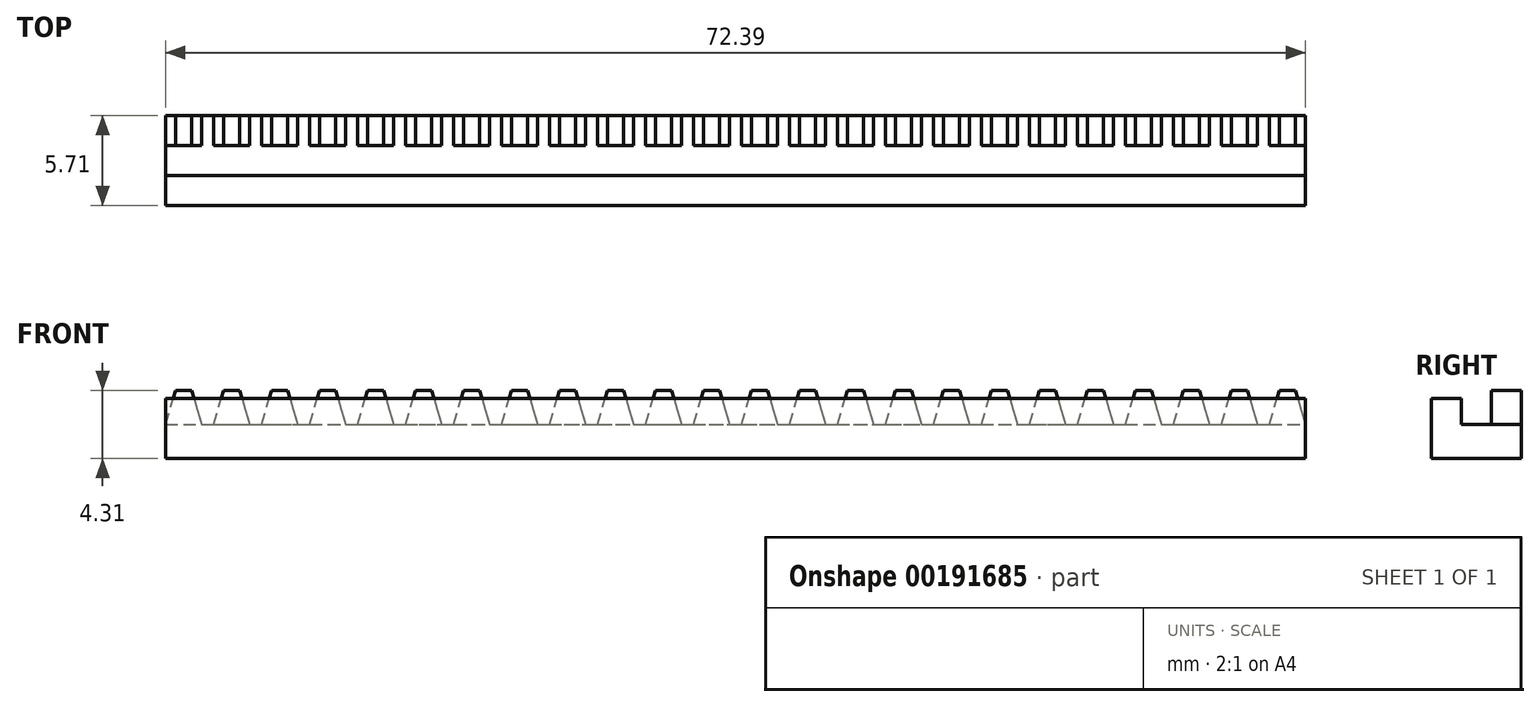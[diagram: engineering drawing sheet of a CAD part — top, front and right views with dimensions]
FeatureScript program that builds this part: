
annotation { "Feature Type Name" : "Feature", "Feature Type Description" : "" }
export const myFeature = defineFeature(function(context is Context, id is Id, definition is map)
    precondition{}
    {
        {
            var Q0;
            Q0=qCreatedBy(makeId("Front.planeOp"),FACE);
            var sketch = newSketch(context, id + "F0", { "sketchPlane" : qUnion([Q0])});
            skLineSegment(sketch, "E0.top", {"start": v(-38.44, 16.9) * mm, "end": v(33.18, 16.9) * mm});
            skLineSegment(sketch, "E0.left", {"start": v(-38.44, 12.58) * mm, "end": v(-38.44, 16.9) * mm});
            skLineSegment(sketch, "E1", {"start": v(-38.44, 16.9) * mm, "end": v(-37.17, 21.21) * mm});
            skLineSegment(sketch, "E2", {"start": v(-37.17, 21.21) * mm, "end": v(-35.14, 21.21) * mm});
            skLineSegment(sketch, "E3", {"start": v(-35.14, 21.21) * mm, "end": v(-33.87, 16.9) * mm});
            skLineSegment(sketch, "E4", {"start": v(-38.44, 16.9) * mm, "end": v(-33.87, 16.9) * mm});
            skLineSegment(sketch, "E5", {"start": v(-36.16, 21.21) * mm, "end": v(-36.16, 16.9) * mm, "construction": true});
            skLineSegment(sketch, "E6.1.0.0", {"start": v(-29.05, 21.21) * mm, "end": v(-27.78, 16.9) * mm});
            skLineSegment(sketch, "E6.1.0.1", {"start": v(-32.35, 16.9) * mm, "end": v(-31.08, 21.21) * mm});
            skLineSegment(sketch, "E6.1.0.2", {"start": v(-31.08, 21.21) * mm, "end": v(-29.05, 21.21) * mm});
            skLineSegment(sketch, "E6.2.0.0", {"start": v(-22.95, 21.21) * mm, "end": v(-21.68, 16.9) * mm});
            skLineSegment(sketch, "E6.2.0.1", {"start": v(-26.25, 16.9) * mm, "end": v(-24.98, 21.21) * mm});
            skLineSegment(sketch, "E6.2.0.2", {"start": v(-24.98, 21.21) * mm, "end": v(-22.95, 21.21) * mm});
            skLineSegment(sketch, "E6.3.0.0", {"start": v(-16.85, 21.21) * mm, "end": v(-15.58, 16.9) * mm});
            skLineSegment(sketch, "E6.3.0.1", {"start": v(-20.16, 16.9) * mm, "end": v(-18.89, 21.21) * mm});
            skLineSegment(sketch, "E6.3.0.2", {"start": v(-18.89, 21.21) * mm, "end": v(-16.85, 21.21) * mm});
            skLineSegment(sketch, "E6.4.0.0", {"start": v(-10.76, 21.21) * mm, "end": v(-9.49, 16.9) * mm});
            skLineSegment(sketch, "E6.4.0.1", {"start": v(-14.06, 16.9) * mm, "end": v(-12.8, 21.21) * mm});
            skLineSegment(sketch, "E6.4.0.2", {"start": v(-12.8, 21.21) * mm, "end": v(-10.76, 21.21) * mm});
            skLineSegment(sketch, "E6.5.0.0", {"start": v(-4.66, 21.21) * mm, "end": v(-3.4, 16.9) * mm});
            skLineSegment(sketch, "E6.5.0.1", {"start": v(-7.96, 16.9) * mm, "end": v(-6.7, 21.21) * mm});
            skLineSegment(sketch, "E6.5.0.2", {"start": v(-6.7, 21.21) * mm, "end": v(-4.66, 21.21) * mm});
            skLineSegment(sketch, "E6.6.0.0", {"start": v(1.43, 21.21) * mm, "end": v(2.7, 16.9) * mm});
            skLineSegment(sketch, "E6.6.0.1", {"start": v(-1.87, 16.9) * mm, "end": v(-0.6, 21.21) * mm});
            skLineSegment(sketch, "E6.6.0.2", {"start": v(-0.6, 21.21) * mm, "end": v(1.43, 21.21) * mm});
            skLineSegment(sketch, "E6.7.0.0", {"start": v(7.53, 21.21) * mm, "end": v(8.8, 16.9) * mm});
            skLineSegment(sketch, "E6.7.0.1", {"start": v(4.23, 16.9) * mm, "end": v(5.5, 21.21) * mm});
            skLineSegment(sketch, "E6.7.0.2", {"start": v(5.5, 21.21) * mm, "end": v(7.53, 21.21) * mm});
            skLineSegment(sketch, "E6.8.0.0", {"start": v(13.63, 21.21) * mm, "end": v(14.9, 16.9) * mm});
            skLineSegment(sketch, "E6.8.0.1", {"start": v(10.32, 16.9) * mm, "end": v(11.6, 21.21) * mm});
            skLineSegment(sketch, "E6.8.0.2", {"start": v(11.6, 21.21) * mm, "end": v(13.63, 21.21) * mm});
            skLineSegment(sketch, "E6.9.0.0", {"start": v(19.72, 21.21) * mm, "end": v(21, 16.9) * mm});
            skLineSegment(sketch, "E6.9.0.1", {"start": v(16.42, 16.9) * mm, "end": v(17.69, 21.21) * mm});
            skLineSegment(sketch, "E6.9.0.2", {"start": v(17.69, 21.21) * mm, "end": v(19.72, 21.21) * mm});
            skLineSegment(sketch, "E6.10.0.0", {"start": v(25.82, 21.21) * mm, "end": v(27.09, 16.9) * mm});
            skLineSegment(sketch, "E6.10.0.1", {"start": v(22.52, 16.9) * mm, "end": v(23.79, 21.21) * mm});
            skLineSegment(sketch, "E6.10.0.2", {"start": v(23.79, 21.21) * mm, "end": v(25.82, 21.21) * mm});
            skLineSegment(sketch, "E6.11.0.0", {"start": v(31.91, 21.21) * mm, "end": v(33.18, 16.9) * mm});
            skLineSegment(sketch, "E6.11.0.1", {"start": v(28.61, 16.9) * mm, "end": v(29.88, 21.21) * mm});
            skLineSegment(sketch, "E6.11.0.2", {"start": v(29.88, 21.21) * mm, "end": v(31.91, 21.21) * mm});
            skLineSegment(sketch, "E6.direction1", {"start": v(-38.44, 16.9) * mm, "end": v(-32.35, 16.9) * mm, "construction": true});
            skPoint(sketch, "E7.centerSnap0", {"position": v(-38.44, 14.74) * mm});
            skLineSegment(sketch, "E8.0.12.0", {"start": v(38, 21.21) * mm, "end": v(39.28, 16.9) * mm});
            skLineSegment(sketch, "E8.3.12.0", {"start": v(34.7, 16.9) * mm, "end": v(35.98, 21.21) * mm});
            skLineSegment(sketch, "E8.6.12.0", {"start": v(35.98, 21.21) * mm, "end": v(38, 21.21) * mm});
            skLineSegment(sketch, "E8.0.13.0", {"start": v(44.1, 21.21) * mm, "end": v(45.38, 16.9) * mm});
            skLineSegment(sketch, "E8.3.13.0", {"start": v(40.8, 16.9) * mm, "end": v(42.07, 21.21) * mm});
            skLineSegment(sketch, "E8.6.13.0", {"start": v(42.07, 21.21) * mm, "end": v(44.1, 21.21) * mm});
            skLineSegment(sketch, "E8.0.14.0", {"start": v(50.2, 21.21) * mm, "end": v(51.47, 16.9) * mm});
            skLineSegment(sketch, "E8.3.14.0", {"start": v(46.9, 16.9) * mm, "end": v(48.17, 21.21) * mm});
            skLineSegment(sketch, "E8.6.14.0", {"start": v(48.17, 21.21) * mm, "end": v(50.2, 21.21) * mm});
            skLineSegment(sketch, "E8.0.15.0", {"start": v(56.3, 21.21) * mm, "end": v(57.57, 16.9) * mm});
            skLineSegment(sketch, "E8.3.15.0", {"start": v(53, 16.9) * mm, "end": v(54.27, 21.21) * mm});
            skLineSegment(sketch, "E8.6.15.0", {"start": v(54.27, 21.21) * mm, "end": v(56.3, 21.21) * mm});
            skLineSegment(sketch, "E8.0.16.0", {"start": v(62.4, 21.21) * mm, "end": v(63.66, 16.9) * mm});
            skLineSegment(sketch, "E8.3.16.0", {"start": v(59.1, 16.9) * mm, "end": v(60.36, 21.21) * mm});
            skLineSegment(sketch, "E8.6.16.0", {"start": v(60.36, 21.21) * mm, "end": v(62.4, 21.21) * mm});
            skLineSegment(sketch, "E8.0.17.0", {"start": v(68.49, 21.21) * mm, "end": v(69.76, 16.9) * mm});
            skLineSegment(sketch, "E8.3.17.0", {"start": v(65.19, 16.9) * mm, "end": v(66.46, 21.21) * mm});
            skLineSegment(sketch, "E8.6.17.0", {"start": v(66.46, 21.21) * mm, "end": v(68.49, 21.21) * mm});
            skLineSegment(sketch, "E8.0.18.0", {"start": v(74.59, 21.21) * mm, "end": v(75.86, 16.9) * mm});
            skLineSegment(sketch, "E8.3.18.0", {"start": v(71.28, 16.9) * mm, "end": v(72.55, 21.21) * mm});
            skLineSegment(sketch, "E8.6.18.0", {"start": v(72.55, 21.21) * mm, "end": v(74.59, 21.21) * mm});
            skLineSegment(sketch, "E8.0.19.0", {"start": v(80.68, 21.21) * mm, "end": v(81.95, 16.9) * mm});
            skLineSegment(sketch, "E8.3.19.0", {"start": v(77.38, 16.9) * mm, "end": v(78.65, 21.21) * mm});
            skLineSegment(sketch, "E8.6.19.0", {"start": v(78.65, 21.21) * mm, "end": v(80.68, 21.21) * mm});
            skLineSegment(sketch, "E8.0.20.0", {"start": v(86.78, 21.21) * mm, "end": v(88.05, 16.9) * mm});
            skLineSegment(sketch, "E8.3.20.0", {"start": v(83.48, 16.9) * mm, "end": v(84.75, 21.21) * mm});
            skLineSegment(sketch, "E8.6.20.0", {"start": v(84.75, 21.21) * mm, "end": v(86.78, 21.21) * mm});
            skLineSegment(sketch, "E8.0.21.0", {"start": v(92.87, 21.21) * mm, "end": v(94.14, 16.9) * mm});
            skLineSegment(sketch, "E8.3.21.0", {"start": v(89.57, 16.9) * mm, "end": v(90.84, 21.21) * mm});
            skLineSegment(sketch, "E8.6.21.0", {"start": v(90.84, 21.21) * mm, "end": v(92.87, 21.21) * mm});
            skLineSegment(sketch, "E8.0.22.0", {"start": v(98.97, 21.21) * mm, "end": v(100.24, 16.9) * mm});
            skLineSegment(sketch, "E8.3.22.0", {"start": v(95.67, 16.9) * mm, "end": v(96.94, 21.21) * mm});
            skLineSegment(sketch, "E8.6.22.0", {"start": v(96.94, 21.21) * mm, "end": v(98.97, 21.21) * mm});
            skLineSegment(sketch, "E8.0.23.0", {"start": v(105.07, 21.21) * mm, "end": v(106.34, 16.9) * mm});
            skLineSegment(sketch, "E8.3.23.0", {"start": v(101.76, 16.9) * mm, "end": v(103.03, 21.21) * mm});
            skLineSegment(sketch, "E8.6.23.0", {"start": v(103.03, 21.21) * mm, "end": v(105.07, 21.21) * mm});
            skLineSegment(sketch, "E9", {"start": v(33.18, 16.9) * mm, "end": v(106.34, 16.9) * mm});
            skLineSegment(sketch, "E10", {"start": v(-38.44, 12.58) * mm, "end": v(106.34, 12.58) * mm});
            skLineSegment(sketch, "E11", {"start": v(106.34, 12.58) * mm, "end": v(106.34, 16.9) * mm});
            skSolve(sketch);
        }
        {
            var Q0;
            Q0=qSketchRegion(id+"F0",true);
            extrude(context, id + "F1", {"entities" : qUnion([Q0]), "depth" : 3.8 * mm});
        }
        {
            var Q0;
            Q0=qCreatedBy(makeId("Right.planeOp"),FACE);
            var Q1;
            Q1=makeQuery(id+"F1.opExtrude","CAP_VERTEX",VERTEX,{"disambiguationData":[OSD([sQuery(id+"F0.wireOp",EDGE,"E10"),sQuery(id+"F0.wireOp",EDGE,"E11")])],"isStart":false});
            cPlane(context, id + "F2", {"entities" : qUnion([Q0, Q1]), "cplaneType" : CPlaneType.PLANE_POINT, "offset" : 25.4 * mm, "width" : 152.4 * mm, "height" : 152.4 * mm});
        }
        {
            var Q0;
            Q0=qCreatedBy(id+"F2.planeOp",FACE);
            var sketch = newSketch(context, id + "F3", { "sketchPlane" : qUnion([Q0])});
            skLineSegment(sketch, "E12", {"start": v(-15.24, 16.39) * mm, "end": v(-11.43, 16.39) * mm});
            skLineSegment(sketch, "E13", {"start": v(-7.62, 16.9) * mm, "end": v(-7.62, 20.2) * mm});
            skLineSegment(sketch, "E14", {"start": v(-7.62, 20.2) * mm, "end": v(-11.43, 20.2) * mm});
            skLineSegment(sketch, "E15", {"start": v(-11.43, 20.2) * mm, "end": v(-11.43, 16.39) * mm});
            skLineSegment(sketch, "E16", {"start": v(-3.81, 12.58) * mm, "end": v(-15.24, 12.58) * mm});
            skLineSegment(sketch, "E17", {"start": v(-15.24, 12.58) * mm, "end": v(-15.24, 16.39) * mm});
            skLineSegment(sketch, "E18.0", {"start": v(-3.81, 12.58) * mm, "end": v(-3.81, 16.9) * mm});
            skLineSegment(sketch, "E19", {"start": v(-3.81, 16.9) * mm, "end": v(-7.62, 16.9) * mm});
            skLineSegment(sketch, "E20", {"start": v(-11.43, 16.39) * mm, "end": v(-11.43, 12.58) * mm});
            skSolve(sketch);
        }
        {
            var Q0;
            Q0=makeQuery(id+"F3.imprint","IMPRINT",FACE,{"disambiguationData":[TD([[makeQuery(id+"F3.imprint","IMPRINT",EDGE,{"derivedFrom":sQuery(id+"F3.wireOp",EDGE,"E13")}),1.0]])]});
            var Q1;
            Q1=makeQuery(id+"F1.opExtrude","SWEPT_FACE",FACE,{"disambiguationData":[OSD([sQuery(id+"F0.wireOp",EDGE,"E0.left")])]});
            extrude(context, id + "F4", {"entities" : qUnion([Q0]), "operationType" : NewBodyOperationType.ADD, "endBound" : BoundingType.UP_TO_SURFACE, "oppositeDirection" : true, "endBoundEntityFace" : qUnion([Q1]), "depth" : 33.02 * mm});
        }
        {
            var Q0;
            Q0=makeQuery(id+"F1.opExtrude","SWEPT_BODY",BODY,{"disambiguationData":[OSD([sQuery(id+"F0.wireOp",EDGE,"E0.top"),sQuery(id+"F0.wireOp",EDGE,"E0.left"),sQuery(id+"F0.wireOp",EDGE,"E1"),sQuery(id+"F0.wireOp",EDGE,"E2"),sQuery(id+"F0.wireOp",EDGE,"E3"),sQuery(id+"F0.wireOp",EDGE,"E6.1.0.0"),sQuery(id+"F0.wireOp",EDGE,"E6.1.0.1"),sQuery(id+"F0.wireOp",EDGE,"E6.1.0.2"),sQuery(id+"F0.wireOp",EDGE,"E6.2.0.0"),sQuery(id+"F0.wireOp",EDGE,"E6.2.0.1"),sQuery(id+"F0.wireOp",EDGE,"E6.2.0.2"),sQuery(id+"F0.wireOp",EDGE,"E6.3.0.0"),sQuery(id+"F0.wireOp",EDGE,"E6.3.0.1"),sQuery(id+"F0.wireOp",EDGE,"E6.3.0.2"),sQuery(id+"F0.wireOp",EDGE,"E6.4.0.0"),sQuery(id+"F0.wireOp",EDGE,"E6.4.0.1"),sQuery(id+"F0.wireOp",EDGE,"E6.4.0.2"),sQuery(id+"F0.wireOp",EDGE,"E6.5.0.0"),sQuery(id+"F0.wireOp",EDGE,"E6.5.0.1"),sQuery(id+"F0.wireOp",EDGE,"E6.5.0.2"),sQuery(id+"F0.wireOp",EDGE,"E6.6.0.0"),sQuery(id+"F0.wireOp",EDGE,"E6.6.0.1"),sQuery(id+"F0.wireOp",EDGE,"E6.6.0.2"),sQuery(id+"F0.wireOp",EDGE,"E6.7.0.0"),sQuery(id+"F0.wireOp",EDGE,"E6.7.0.1"),sQuery(id+"F0.wireOp",EDGE,"E6.7.0.2"),sQuery(id+"F0.wireOp",EDGE,"E6.8.0.0"),sQuery(id+"F0.wireOp",EDGE,"E6.8.0.1"),sQuery(id+"F0.wireOp",EDGE,"E6.8.0.2"),sQuery(id+"F0.wireOp",EDGE,"E6.9.0.0"),sQuery(id+"F0.wireOp",EDGE,"E6.9.0.1"),sQuery(id+"F0.wireOp",EDGE,"E6.9.0.2"),sQuery(id+"F0.wireOp",EDGE,"E6.10.0.0"),sQuery(id+"F0.wireOp",EDGE,"E6.10.0.1"),sQuery(id+"F0.wireOp",EDGE,"E6.10.0.2"),sQuery(id+"F0.wireOp",EDGE,"E6.11.0.0"),sQuery(id+"F0.wireOp",EDGE,"E6.11.0.1"),sQuery(id+"F0.wireOp",EDGE,"E6.11.0.2"),sQuery(id+"F0.wireOp",EDGE,"E8.0.12.0"),sQuery(id+"F0.wireOp",EDGE,"E8.3.12.0"),sQuery(id+"F0.wireOp",EDGE,"E8.6.12.0"),sQuery(id+"F0.wireOp",EDGE,"E8.0.13.0"),sQuery(id+"F0.wireOp",EDGE,"E8.3.13.0"),sQuery(id+"F0.wireOp",EDGE,"E8.6.13.0"),sQuery(id+"F0.wireOp",EDGE,"E8.0.14.0"),sQuery(id+"F0.wireOp",EDGE,"E8.3.14.0"),sQuery(id+"F0.wireOp",EDGE,"E8.6.14.0"),sQuery(id+"F0.wireOp",EDGE,"E8.0.15.0"),sQuery(id+"F0.wireOp",EDGE,"E8.3.15.0"),sQuery(id+"F0.wireOp",EDGE,"E8.6.15.0"),sQuery(id+"F0.wireOp",EDGE,"E8.0.16.0"),sQuery(id+"F0.wireOp",EDGE,"E8.3.16.0"),sQuery(id+"F0.wireOp",EDGE,"E8.6.16.0"),sQuery(id+"F0.wireOp",EDGE,"E8.0.17.0"),sQuery(id+"F0.wireOp",EDGE,"E8.3.17.0"),sQuery(id+"F0.wireOp",EDGE,"E8.6.17.0"),sQuery(id+"F0.wireOp",EDGE,"E8.0.18.0"),sQuery(id+"F0.wireOp",EDGE,"E8.3.18.0"),sQuery(id+"F0.wireOp",EDGE,"E8.6.18.0"),sQuery(id+"F0.wireOp",EDGE,"E8.0.19.0"),sQuery(id+"F0.wireOp",EDGE,"E8.3.19.0"),sQuery(id+"F0.wireOp",EDGE,"E8.6.19.0"),sQuery(id+"F0.wireOp",EDGE,"E8.0.20.0"),sQuery(id+"F0.wireOp",EDGE,"E8.3.20.0"),sQuery(id+"F0.wireOp",EDGE,"E8.6.20.0"),sQuery(id+"F0.wireOp",EDGE,"E8.0.21.0"),sQuery(id+"F0.wireOp",EDGE,"E8.3.21.0"),sQuery(id+"F0.wireOp",EDGE,"E8.6.21.0"),sQuery(id+"F0.wireOp",EDGE,"E8.0.22.0"),sQuery(id+"F0.wireOp",EDGE,"E8.3.22.0"),sQuery(id+"F0.wireOp",EDGE,"E8.6.22.0"),sQuery(id+"F0.wireOp",EDGE,"E8.0.23.0"),sQuery(id+"F0.wireOp",EDGE,"E8.3.23.0"),sQuery(id+"F0.wireOp",EDGE,"E8.6.23.0"),sQuery(id+"F0.wireOp",EDGE,"E9"),sQuery(id+"F0.wireOp",EDGE,"E10"),sQuery(id+"F0.wireOp",EDGE,"E11")])]});
            var Q1;
            Q1=makeQuery(id+"F1.opExtrude","CAP_VERTEX",VERTEX,{"disambiguationData":[OSD([sQuery(id+"F0.wireOp",EDGE,"E0.left"),sQuery(id+"F0.wireOp",EDGE,"E10")])],"isStart":true});
            transform(context, id + "F5", {"entities" : qUnion([Q0]), "transformType" : TransformType.SCALE_UNIFORMLY, "scale" : .5, "scalePoint" : qUnion([Q1]), "makeCopy" : false});
        }
    });
